# Revit family: 0010280
name_source: partatom
category: Lighting Fixtures
revit_build: Autodesk Revit 2017 (Build: 20190507_1515(x64)
units: mm (PartAtom-declared; Revit-internal decimal feet)

## family parameters
Cut with Voids When Loaded = No
Host = Face
Light Source = Yes
OmniClass Number = 23.80.70.00
OmniClass Title = Lighting
Part Type = Normal
Room Calculation Point = No
Round Connector Dimension = Use Diameter
Shared = No

## types (4) — shared parameters
Assembly Code = D5020200
AssetType = Fixed
BODY_SYL = 36 mm  [stored 0.11811 ft]
BRACKET_HEIGHT_SYL = 9 mm  [stored 0.0295276 ft]
CHAMFER_SYL = 19 mm
ClassificationName = Uniclass2015
ClassificationValue = EF_70_80
Color Filter = 16777215
DIF_HEIGHT_SYL = 24 mm
DIF_WIDHT_SYL = 35 mm  [stored 0.114829 ft]
Default Elevation = 1219 mm
Dimming Lamp Color Temperature Shift = <None>
DocumentationLiterature = http://www.sylvania-lighting.com
ElectricShockClassification = Class I
Emit Shape Visible in Rendering = No
Emit from Circle Diameter = 610 mm
IfcExportAs = IfcLightFixtureType
IfcExportType = IfcLightFixtureType
ImpactProtectionIndex = IK08
IngressProtection = IP66
Keynote = 16500
L0650_SYL = No
LEGHT_1200-_SYL = -600 mm
LEGHT_1200_SYL = 600 mm
LEGHT_1500-_SYL = -750 mm
LEGHT_1500_SYL = 750 mm
LEGHT_650-_SYL = -325 mm
LENGHT_650_SYL = 325 mm
Lamp = LED
LampColourRenderingIndex = 80
LampColourTemperature = 4000 K
LampMacAdamStep = 3
LampsType = LED
MID_WIDTH_SYL = 36 mm  [stored 0.11811 ft]
Manufacturer = Feilo Sylvania
ManufacturerName = Feilo Sylvania
Material = pc polycarbonate housing, pc polycarbonate diffuser
Material_1_SYL = Default
Material_2_SYL = <By Category>
Material_3_SYL = <By Category>
Material_4_SYL = <By Category>
NominalDepth = 87 mm
NominalHeight = 80 mm
TOP_WIDTH_SYL = 34 mm
Tilt Angle = -90.00°
Type Image = <None>
URL = http://www.sylvania-lighting.com
Voltage = 0 V
WIDTH_SYL = 45 mm
zero-valued in all types: Cost

## per-type parameters (varying)
| type | Apparent Load | BRACKET_DIST_SYL | BRACKET_WIDTH_SYL | Description | L1200_SYL | L1500_SYL | LENGHT-_CHAMFER_SYL | LENGHT-_SYL | LENGHT_CHAMFER_SYL | LENGHT_SYL | LampNominalLuminous | LuminousEfficacy | Model | ModelNumber | ModelReference | Name | NominalLength | Photometric Web File | PowerConsumption | PowerFactor | TypeName |
| 0010283 RESISTO 1500 HE IP66 DALI 7100LM 840 EM | 50 VA | 594 mm | 550 mm | Resisto, integrated LED weatherproof luminaire, with UV stabilized flat diffuser designed to achieve uniform lit appearance, optimise light output and to reduce glare. 301 stainless steel diffuser clips and fixing brackets for surface mounting. Polycarbonate housing and diffuser - no yellow discolouration over time. 7100lm; 50W; 142lm/W; 4000K; SDCM<3; DALI dimmable; CRI80; IP66; IK08; Class I; 69,000hrs (L80B20) lifespan; 1500mm x 89mm x 88mm; D-mark; 3-hour maintained emergency batteries. | No | Yes | -750 mm | -742 mm | 750 mm | 742 mm | 7100 lm | 142 lm/W | Resisto 1500 HE IP66 DALI 7100LM 840 EM | 0010283 | Resisto 1500 HE IP66 DALI 7100LM 840 EM | Resisto 1500 HE IP66 DALI 7100LM 840 EM | 1500 mm | 0010283.ies | 50 W | 0.98 | Resisto 1500 HE IP66 DALI 7100LM 840 EM |
| 0010282 RESISTO 1500 HE IP66 DALI 4000LM 840 EM | 29 VA | 594 mm | 550 mm | Resisto, integrated LED weatherproof luminaire, with UV stabilized flat diffuser designed to achieve uniform lit appearance, optimise light output and to reduce glare. 301 stainless steel diffuser clips and fixing brackets for surface mounting. Polycarbonate housing and diffuser - no yellow discolouration over time. 4000lm; 29W; 138lm/W; 4000K; SDCM<3; DALI dimmable; CRI80; IP66; IK08; Class I; 69,000hrs (L80B20) lifespan; 1500mm x 89mm x 88mm; D-mark; 3-hour maintained emergency batteries. | No | Yes | -750 mm | -742 mm | 750 mm | 742 mm | 4000 lm | 138 lm/W | Resisto 1500 HE IP66 DALI 4000LM 840 EM | 0010282 | Resisto 1500 HE IP66 DALI 4000LM 840 EM | Resisto 1500 HE IP66 DALI 4000LM 840 EM | 1500 mm | 0010282.ies | 29 W | 0.98 | Resisto 1500 HE IP66 DALI 4000LM 840 EM |
| 0010281 RESISTO 1200 HE IP66 DALI 4800LM 840 EM | 35 VA | 444 mm | 400 mm  [stored 1.31234 ft] | Resisto, integrated LED weatherproof luminaire, with UV stabilized flat diffuser designed to achieve uniform lit appearance, optimise light output and to reduce glare. 301 stainless steel diffuser clips and fixing brackets for surface mounting. Polycarbonate housing and diffuser - no yellow discolouration over time. 4800lm; 35W; 137lm/W; 4000K; SDCM<3; DALI dimmable; CRI80; IP66; IK08; Class I; 69,000hrs (L80B20) lifespan; 1200mm x 89mm x 88mm; D-mark; 3-hour maintained emergency batteries. | Yes | No | -600 mm | -592 mm  [stored -1.94226 ft] | 600 mm | 592 mm  [stored 1.94226 ft] | 4800 lm | 137 lm/W | Resisto 1200 HE IP66 DALI 4800LM 840 EM | 0010281 | Resisto 1200 HE IP66 DALI 4800LM 840 EM | Resisto 1200 HE IP66 DALI 4800LM 840 EM | 1200 mm | 0010281.ies | 35 W | 0.98 | Resisto 1200 HE IP66 DALI 4800LM 840 EM |
| 0010280 RESISTO 1200 HE IP66 DALI 2800LM 840 EM | 22 VA | 444 mm | 400 mm  [stored 1.31234 ft] | Resisto, integrated LED weatherproof luminaire, with UV stabilized flat diffuser designed to achieve uniform lit appearance, optimise light output and to reduce glare. 301 stainless steel diffuser clips and fixing brackets for surface mounting. Polycarbonate housing and diffuser - no yellow discolouration over time. 2800lm; 22W; 127lm/W; 4000K; SDCM<3; DALI dimmable; CRI80; IP66; IK08; Class I; 69,000hrs (L80B20) lifespan; 1200mm x 89mm x 88mm; D-mark; 3-hour maintained emergency batteries. | Yes | No | -600 mm | -592 mm  [stored -1.94226 ft] | 600 mm | 592 mm  [stored 1.94226 ft] | 2800 lm | 127 lm/W | Resisto 1200 HE IP66 DALI 2800LM 840 EM | 0010280 | Resisto 1200 HE IP66 DALI 2800LM 840 EM | Resisto 1200 HE IP66 DALI 2800LM 840 EM | 1200 mm | 0010280.ies | 22 W | 1 | Resisto 1200 HE IP66 DALI 2800LM 840 EM |

note: [stored X ft] marks values corroborated as IEEE doubles in the binary element streams (Revit-internal decimal feet)

## geometry (parser evidence)
native form markers: Sweep x3
no freeform markers — native parametric forms only
